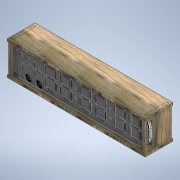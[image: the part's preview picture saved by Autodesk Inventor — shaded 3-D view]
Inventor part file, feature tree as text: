
AUTODESK INVENTOR PART (.ipt)
format: ipt  version: 2021 (Build 250183000, 183)  size: 3,604,992 bytes
history: native  units: in
note: dims shown in document units (in); Inventor stores cm internally (conversion verified against a paired STEP export)
features: other x71, extrude x21, sketch x21, hole x1, imported_body x1
ambient origin geometry x8: Origin, YZ Plane, XZ Plane, XY Plane, X Axis, Y Axis, Z Axis, Center Point
bodies: Body1 (feature_tree), Body2 (feature_tree), Body3 (feature_tree), Body4 (feature_tree), Body5 (feature_tree), Body6 (feature_tree), Body7 (feature_tree)
feature tree (115):
  other  "Clock Face"
  other  "Blocks"
  extrude  "Extrusion1"  TaperAngle=135.0deg  [1 undecoded]
  extrude  "Extrusion3"  TaperAngle=135.0deg  [1 undecoded]
  extrude  "Extrusion5"  Depth=0.0433in
  extrude  "Extrusion6"  Depth=0.0433in
  extrude  "Extrusion9"  Depth=0.0433in
  extrude  "Extrusion7"  Depth=0.0433in
  extrude  "Extrusion10"  Depth=0.0433in
  extrude  "Extrusion8"  Depth=0.0433in
  hole  "Hole1"  [1 undecoded]
  extrude  "Extrusion26"  Depth=0.126in
  extrude  "Extrusion27"  Depth=2.2441in
  extrude  "Extrusion28"  Depth=0.126in
  extrude  "Base Extrusion"  Depth=0.126in
  extrude  "Side Extrusion"  Depth=0.1969in
  extrude  "Extrusion16"  Depth=0.0866in
  extrude  "Extrusion22"  Depth=0.0118in
  extrude  "Extrusion23"  Depth=0.0118in
  extrude  "Extrusion17"  Depth=0.1969in
  extrude  "Lid Extrusion"  Depth=0.6693in
  extrude  "Extrusion19"  Depth=0.2953in
  extrude  "Extrusion20"  Depth=0.2953in
  extrude  "Extrusion21"  TaperAngle=0.0deg  [1 undecoded]
  other  "Single Segment"
  other  "7 Segment Digit"
  other  "Slanted Segment Large"
  other  "+ sign"
  other  "Dot"
  other  "Clock Face with T +-"
  other  "Clock Front Face Outline"
  other  "Small Segmemt"
  sketch  "Sketch5"  dims[d10=62.9921in d11=78.7402in d29=0.1181in d30=0.0in]
  sketch  "Sketch8"  dims[d105=0.0866in d108=0.0866in d111=0.0866in d112=0.0866in d113=0.0866in d114=0.0866in d115=0.0866in d116=0.0394in d117=0.1969in d121=0.0866in d122=0.0866in d126=135.0deg]
  other  "ClockBackface"
  sketch  "Sketch9"  dims[d127=0.8661in d128=135.0deg]
  sketch  "Sketch10"  dims[d129=0.0984in]
  other  "Backplace"
  sketch  "Sketch11"  dims[d131=0.0433in d132=0.0433in d137=0.0433in d138=0.0433in d139=0.0433in d140=0.0433in]
  other  "FrontCover"
  other  "7SegmentOutline"
  sketch  "Sketch15"  dims[d141=0.0433in d142=0.0433in]
  other  "Cable Trench"
  other  "Cable Trench Long"
  other  "CableCutouts"
  sketch  "Sketch17"  dims[d143=0.0433in d144=0.0433in]
  sketch  "Sketch20"  dims[d145=0.0433in d146=0.0433in]
  imported_body  "Base"
  sketch  "Sketch21"  dims[d150=0.0433in d151=0.0433in]
  other  "Side Panels"
  sketch  "Sketch23"  dims[d152=0.0433in d153=0.0433in]
  sketch  "Sketch25"  dims[d294=0.126in d295=0.126in]
  sketch  "Sketch26"  dims[d296=0.315in d297=0.126in]
  other  "Top Panel"
  sketch  "Sketch27"  dims[d298=0.126in d299=2.2441in]
  sketch  "Sketch28"  dims[d304=0.126in d305=0.126in]
  sketch  "Sketch29"  dims[d306=0.126in d307=0.126in]
  sketch  "Sketch30"  dims[d311=0.0787in d312=0.0787in d314=0.0787in d315=0.0787in d316=0.0787in d317=0.0787in d318=0.0787in d319=0.0787in d320=0.0394in d321=0.0394in d322=0.0394in d323=0.0394in d348=0.1969in]
  sketch  "Sketch31"  dims[d349=0.8661in d350=0.0866in]
  sketch  "Sketch32"  dims[d352=0.0118in d353=0.0118in]
  sketch  "Sketch35"  dims[d358=0.0118in d359=0.0118in]
  sketch  "Sketch36"  dims[d360=0.1969in d361=0.1969in]
  sketch  "Sketch37"  dims[d362=0.2953in d363=0.6693in d364=0.2953in d366=0.2953in d367=0.0in d368=0.0in d369=0.0in d370=0.0in d371=0.0in d372=0.5906in d373=0.0in d374=0.6299in d375=0.2362in d376=0.2362in d377=0.5354in d378=0.6299in d379=0.2362in d380=0.5906in d381=0.0in d402=1.9528in d429=12.9921in d430=2.7559in d431=0.9843in d462=0.0866in d463=0.0866in d464=0.0866in d465=0.0866in d466=0.0866in d467=0.0866in d468=0.0866in d469=0.0394in d470=0.1969in d471=0.0866in d472=0.0866in d473=135.0deg d474=0.6299in d475=135.0deg d476=0.0984in d477=0.1969in d478=0.6299in d479=0.0866in d480=0.0118in d481=0.0118in d482=0.0118in d483=0.0118in d496=0.0787in d497=0.0787in d501=0.0394in d502=0.0394in d503=0.0in d504=0.0in d505=0.039in d506=0.039in d507=0.039in d508=0.039in d509=0.8661in d510=0.9843in d511=0.9685in d514=0.0394in d515=0.0394in d516=0.0394in d517=0.0394in d518=0.0in d519=0.039in d520=0.4331in d522=0.9449in d523=0.0in d524=0.0591in d525=0.315in d526=0.2913in d527=0.8661in d528=0.6575in d529=0.315in d530=0.1969in d531=0.0in d536=1.378in d537=6.4961in d538=6.4961in d539=1.378in d542=1.378in d543=6.4961in d544=0.1181in d545=0.0in d549=0.1181in d550=0.0in d551=1.378in d552=6.4961in d553=0.1181in d554=0.0in d555=1.378in d556=6.4961in d557=0.1181in d558=0.0in d564=0.2362in d1135=1.1732in d1136=1.1732in d1137=2.1496in d1138=0.0612in d1139=0.0612in d1140=0.0612in d1143=0.0612in d1144=0.0612in d1145=90.0deg d1146=0.0866in d1147=0.0236in d1150=0.0236in d1153=0.0236in d1154=0.0866in d1155=1.0197in d1156=1.0197in d1157=0.0866in d1158=0.0236in d1159=0.0866in d1160=0.0866in d1161=0.0236in d1162=0.0866in d1163=0.0866in d1164=0.0236in d1165=0.0866in d1166=0.0866in d1167=0.0236in d1168=0.0866in d1169=0.0866in d1170=0.0866in d1171=0.0866in d1172=0.0866in d1173=0.0866in d1175=0.1102in d1176=0.8661in d1177=0.8661in d1178=1.0197in d1179=0.0866in d1180=0.0236in d1181=0.0866in d1182=0.0866in d1183=0.0236in d1184=0.0866in d1188=0.0866in d1189=0.0236in d1190=0.0866in d1193=0.0866in d1194=0.0236in d1195=0.0in d1196=0.0in d1198=135.0deg d1199=0.0612in d1200=0.0866in d1201=0.0in d1202=0.0in d1205=0.0in d1206=0.0in d1207=0.0in d1208=135.0deg d1209=90.0deg d1210=90.0deg d1211=0.0866in d1212=0.0236in d1213=0.6603in d1214=0.6603in d1215=0.6603in d1216=90.0deg d1217=135.0deg d1218=0.6603in d1219=0.0394in d1221=135.0deg d1222=0.0394in d1223=0.0866in d1224=0.0866in d1225=0.0866in d1227=0.0866in d1228=0.0866in d1229=0.0866in d1230=0.0236in d1231=135.0deg d1232=90.0deg d1233=90.0deg d1234=135.0deg d1235=90.0deg d1236=90.0deg d1239=0.1102in d1240=0.2402in d1241=0.2402in d1242=0.2835in d1243=0.2835in d1244=0.2402in d1245=0.2402in d1246=0.0669in d1247=0.0669in d1248=0.0669in d1249=0.0669in d1250=0.0433in d1251=0.0433in d1252=0.8661in d1253=0.1535in d1254=90.0deg d1255=135.0deg d1256=45.0deg d1257=0.6603in d1258=0.0236in d1259=135.0deg d1260=135.0deg d1261=90.0deg d1262=0.0612in d1263=0.0866in d1264=0.0in d1265=0.0in d1266=0.0in d1267=0.0in d1268=0.0in d1269=0.0in d1270=0.0in d1271=0.0in d1272=0.0in d1273=0.0in d1274=0.0in d1275=0.0in d1276=0.0in d1277=0.0in d1278=0.0in d1279=0.0in d1280=0.0in d1281=0.0in d1282=0.0in d1283=0.0in d1292=0.0866in d1307=0.0394in d1308=0.0394in d1309=0.0394in d1310=0.0394in d1311=0.0394in d1312=0.0394in d1313=0.0394in d1314=0.2756in d1315=0.0197in d1316=0.0197in d1317=0.3445in d1318=0.0394in d1319=0.0394in d1320=0.0787in d1321=0.0866in d1322=0.0787in d1323=0.0787in d1344=0.0394in d1350=0.0866in d1351=0.0866in d1386=0.1181in d1387=0.0in d1390=0.0394in d1392=0.0118in d1393=0.0394in d1394=0.0394in d1395=0.0394in d1396=0.0394in d1397=0.1378in d1398=0.1349in d1399=0.0394in d1402=0.0787in d1425=0.0in d1429=0.0in d1431=0.0394in d1432=0.0394in d1507=0.0in d1508=0.0394in d1509=0.0394in d1510=0.0394in d1511=0.0394in d1513=0.0394in d1514=0.0394in d1515=0.0in d1516=0.0in d1517=0.0in d1518=0.0in d1519=0.0197in d1520=0.0197in d1521=0.1969in d1522=0.0394in d1523=0.0394in d1524=0.0394in d1525=0.1181in d1526=0.1181in d1527=0.0394in d1529=0.2741in d1530=0.0787in d1531=0.0787in d1532=0.0325in d1533=0.033in d1534=0.0787in d1535=0.0787in d1536=0.0325in d1537=0.0787in d1538=0.0787in d1539=0.0325in d1635=0.0787in d1636=0.0689in d1638=0.2756in d1641=0.315in d1699=0.0197in d1700=0.0197in d1701=0.3445in d1702=0.0394in d1703=0.0394in d1704=0.0787in d1705=0.0787in d1706=0.0787in d1707=0.0in d1708=0.0394in d1709=0.0394in d1710=0.1462in d1711=0.0in d1712=0.0394in d1713=0.0394in d1714=0.0118in d1715=0.0394in d1716=0.0394in d1717=0.0394in d1718=0.0394in d1719=0.1378in d1720=0.1349in d1721=0.0394in d1722=0.0787in d1723=0.0787in d1724=0.0394in d1725=0.0394in d1726=0.0394in d1727=0.0394in d1728=0.0787in d1729=0.1181in d1730=0.0787in d1731=0.0394in d1732=0.0787in d1733=0.0787in d1734=0.0325in d1735=0.033in d1736=0.0787in d1737=0.0787in d1738=0.0325in d1739=0.0787in d1740=0.0787in d1741=0.0325in d1742=0.0325in d1747=0.2756in d1748=0.0984in d1749=0.0984in d1750=0.315in d1751=0.0325in d1752=0.0787in d1753=0.0787in d1754=0.0394in d1755=0.0394in d1756=0.0394in d1757=0.0394in d1758=0.0394in d1759=0.0394in d1760=0.0394in d1761=0.0394in d1762=0.0in d1763=0.0in d1764=0.0in d1765=0.0in d1766=0.0in d1767=0.0in d1768=0.0in d1769=0.0in d1770=0.1181in d1771=0.1181in d1772=0.4724in d1773=0.2362in d1774=0.0in d1775=0.0in d1776=0.0in d1777=0.0in d1778=0.0in d1779=0.0in d1780=0.0in d1781=0.0in d1782=0.2362in d1783=0.5906in d1784=0.1181in d1785=0.1181in d1786=0.0in d1787=0.0394in d1788=0.0394in d1789=0.0394in d1790=0.0394in d1791=0.0394in d1792=0.0394in d1793=0.0in d1794=0.0in d1795=0.0in d1796=0.0in d1797=0.0197in d1798=0.0197in d1799=0.1969in d1800=0.0394in d1801=0.0394in d1802=0.0394in d1803=0.1181in d1804=0.1181in d1805=0.0394in d1806=0.2741in d1808=0.0394in d1809=0.0394in d1810=0.0394in d1811=0.0394in d1812=0.0394in d1813=0.0394in d1814=0.0394in d1815=0.0394in d1840=0.0787in d1841=0.0787in d1842=0.501in d1843=0.0394in d1844=0.0394in d1845=90.0deg d1846=0.0in d1847=0.0in d1848=0.0in d1849=0.0in d1850=0.0in d1851=0.0in d1852=0.0in d1853=0.0in d1854=0.0in d1855=0.0in d1856=0.0in d1857=0.0in d1858=0.2756in d1859=0.0in d1860=0.0in d1861=0.0in d1862=0.2756in d1863=0.0in d1864=0.1181in d1865=0.0in d1898=0.0394in d1899=0.0591in d1900=0.0591in d1901=0.0591in d1902=0.0591in d1903=0.0591in d1904=0.0591in d1905=0.0394in d1906=0.2559in d1907=0.1772in d1908=0.1772in d1909=0.2559in d1910=0.1575in d1911=0.2362in d1912=0.2393in d1913=0.0197in d1914=0.3051in d1915=0.4066in d1916=0.3051in d1917=0.4066in d1918=0.0886in d1919=0.0689in d1920=0.0886in d1921=0.0in d1923=0.0335in d1924=0.0335in d1925=0.0335in d1926=0.0787in d1927=0.0335in d1940=0.2756in d1943=2.3622in d1944=0.2362in d1945=0.0in d1946=0.2362in d1948=0.0in d1949=0.0in d1950=0.2362in d1954=2.7559in d1955=0.0in d1956=0.1181in d1957=0.1181in d1969=0.0in d1970=0.0in d1971=0.0in d1974=0.0in d1975=0.0in d1976=0.0in d1978=0.2362in d1979=0.0in d1980=0.0197in d1983=0.0in d1984=0.0in d1987=0.0in d1988=0.0in d1989=0.0197in d1990=0.2362in d1991=0.0in d1992=0.2362in d1993=0.0in d1997=0.2362in d2001=0.2362in d2002=0.2362in d2003=0.0in d2004=0.0in d2006=0.3386in d2007=0.3386in d2008=0.2362in d2009=0.0in d2010=0.0in d2011=0.3386in d2012=0.3386in d2013=0.0in d2014=0.0in d2015=0.2362in d2016=0.0in d2017=0.0in d2018=0.0in d2019=0.0in d2020=0.0in d2023=0.0in d2024=0.0in d2027=1.2992in d2030=0.2362in d2032=1.2992in d2035=1.3386in d2041=0.2362in d2042=1.2992in d2043=0.1181in d2044=0.1181in d2045=0.1181in d2046=0.0in d2047=0.1181in d2048=0.1181in d2049=1.2992in d2050=0.1181in d2051=0.0in d2052=0.5906in d2053=0.1693in d2054=0.2362in d2055=0.315in d2056=0.0787in d2057=90.0deg d2058=0.315in d2059=0.8108in d2060=0.315in d2061=0.5906in d2062=0.315in d2063=0.5906in d2064=0.315in d2065=0.5906in d2066=0.315in d2078=0.1181in d2079=0.0in d2080=0.1181in d2081=0.2362in d2082=0.1181in d2083=0.2362in d2084=13.2283in d2085=0.1181in d2086=0.1181in d2087=0.2362in d2089=0.2756in d2090=0.2756in d2091=0.3937in d2092=0.3937in d2093=1.5748in d2094=2.6181in d2095=0.1181in d2096=0.0in d2097=0.0in d2098=0.0in d2099=0.0in d2100=0.0in d2101=0.689in d2102=0.689in d2103=0.1181in d2104=0.0in d2105=0.6299in d2106=0.5512in d2107=0.5512in d2108=0.6299in d2109=0.2953in d2110=0.2953in d2111=0.2756in d2112=0.2756in d2113=0.0197in d2114=0.2362in d2115=0.0in d2116=0.2362in d2117=0.2362in d2118=0.2362in d2119=0.2362in d2120=0.2362in d2121=0.2362in d2123=0.2362in d2124=0.2362in d2125=2.6378in d2126=0.2362in d2127=0.2362in d2128=0.0in d2129=0.0in]
  other  "Single Segment:9"
  other  "Single Segment:10"
  other  "Single Segment:11"
  other  "Single Segment:12"
  other  "Single Segment:13"
  other  "Single Segment:14"
  other  "Single Segment:15"
  other  "7 Segment Digit:8"
  other  "7 Segment Digit:9"
  other  "7 Segment Digit:10"
  other  "7 Segment Digit:11"
  other  "7 Segment Digit:12"
  other  "7 Segment Digit:13"
  other  "Dot:7"
  other  "Dot:8"
  other  "Dot:9"
  other  "Dot:10"
  other  "Clock Front Face Outline:1"
  other  "Small Segmemt:1"
  other  "Small Segmemt:2"
  other  "Small Segmemt:3"
  other  "Small Segmemt:4"
  other  "+ sign:1"
  other  "Small Segmemt:5"
  other  "Small Segmemt:6"
  other  "Small Segmemt:7"
  other  "Small Segmemt:8"
  other  "Clock Face with T +-:1"
  other  "Clock Front Face Outline:2"
  other  "Clock Front Face Outline:3"
  other  "Clock Front Face Outline:4"
  other  "7SegmentOutline:1"
  other  "7SegmentOutline:2"
  other  "7SegmentOutline:3"
  other  "7SegmentOutline:4"
  other  "7SegmentOutline:5"
  other  "7SegmentOutline:6"
  other  "Dot:11"
  other  "Dot:12"
  other  "Dot:13"
  other  "Dot:14"
  other  "Cable Trench:3"
  other  "Cable Trench:4"
  other  "Cable Trench:5"
  other  "Cable Trench Long:4"
  other  "Cable Trench Long:5"
  other  "CableCutouts:3"
  other  "CableCutouts:4"
  other  "CableCutouts:5"
  other  "CableCutouts:6"
  other  "CableCutouts:7"
  other  "CableCutouts:8"
note: 4 required parameter values undecoded (feature->parameter linkage not recoverable at this tier; creation-order binding heuristic only, values carry confidence <= 0.55)
